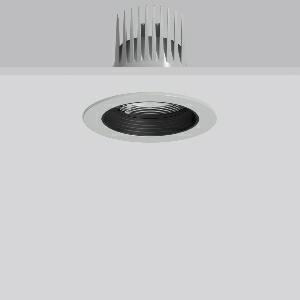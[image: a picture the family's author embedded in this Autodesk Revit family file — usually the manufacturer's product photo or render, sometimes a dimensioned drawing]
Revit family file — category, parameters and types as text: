
# Revit family: heledon_maxi_e_901767_004_3_fd15
name_source: partatom
category: Lighting Fixtures
units: mm (PartAtom-declared; Revit-internal decimal feet)

## family parameters
Cut with Voids When Loaded = No
Host = Face
Light Source = No
Part Type = Normal
Room Calculation Point = No
Round Connector Dimension = Use Diameter
Shared = No

## types (1)
- HELEDON maxi E (1 x LED Modul 935, 3750 lm, 3500)
    Apparent Load = 35 VA
    Approval mark = CE
    CIE Flux Codes = 97 100 100 100 100
    Color Rendering = 92
    Color Temperature = 3500
    Default Elevation = 1800 mm
    Description = Series: HELEDON maxi
Round recessed downlight. Housing: die-cast aluminium, powder-coated. Black plastic ring and recessed LED to prevent glare from the side. Optical assembly with lens made of plastic (polycarbonate) for the best homogeneous light distribution - can be changed without tools. Best colour rendering index Ra>90. Suitable for Recessed ceiling mounting. Installation without tools thanks to spring fastening system. Including separate LED converter with connecting cable 600 mm.High quality converter without flickering and stroboscopic effect. Through-wiring box (5 pole) available as accessory. The following accessories can be mounted without use of tools: interchangeable lenses, decorative glasses, honeycomb louvre, clear and frosted diffusers, white interchangeable plastic ring. 
Colour: silver
Diameter: 162 mm
Height: 3 mm
Cut-out diameter: 152 mm
Recess height: 200 mm
Luminaire: recess height: 135 mm
Lamp: LED
Socket: without socket
Colour temperature: 3500K
Colour rendering index (CRI): 92
System power: 35 W
Rated luminous flux: 3750 lm
Luminous efficiency: 107 lm/W
Control gear: Regulated power supply
Protection class: II
Type of protection: IP 20
    Height = 0 mm  [stored 0 ft]
    Lamp = 1 x LED Modul 935
    Lamp Light Flux = 3750 lm
    Lamp count = 1
    Length = 162 mm
    Lifetime = 50000 h
    Luminous efficacy = 107 lm/W
    Manufacturer = RZB
    ModVariant = No
    Model = 901767.004.3
    Mounting Place = Ceiling
    Mounting Type = Recessed
    Number of Poles = 1
    OnlyDefault = Yes
    Power Factor = 1
    Product Name = HELEDON maxi E
    Product group = Recessed downlights
    ProductGroupID = 402
    Protection Class = Protection class II
    Protection Degree = IP 20
    RLX_Detail_Level = 1
    RLX_Emergency_Light_Flux = 0 lm
    RLX_Emergency_Type = 0
    RLX_Emergency_Type_DB = No
    RlxData = <blob elided: 120493 chars, md5=69daae7b>
    Socket = socket
    Standby Power = 0 W
    System Light Flux = 3750 lm
    System Power = 35 W
    Type Comments = Product without accessories
    Type Image = 901663.004.jpg
    URL = http://relux.com
    VarID = ---
    Voltage = 230 V
    Voltage Range = 220-240 V
    Weight = 0.00 kg
    Width = 0 mm  [stored 0 ft]

note: [stored X ft] marks values corroborated as IEEE doubles in the binary element streams (Revit-internal decimal feet)

## geometry (parser evidence)
native form markers: Blend x4, Sweep x10
no freeform markers — native parametric forms only
